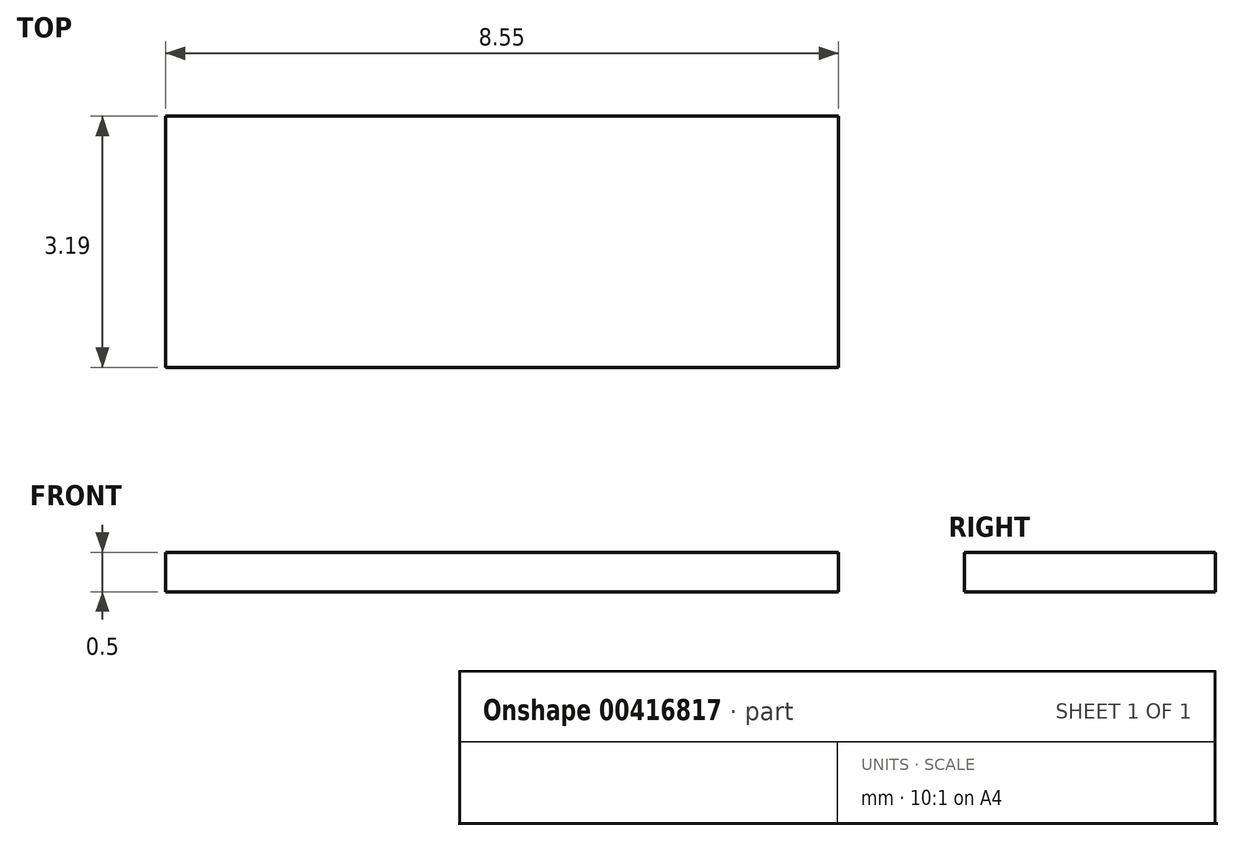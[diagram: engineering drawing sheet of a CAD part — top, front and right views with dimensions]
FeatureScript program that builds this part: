
annotation { "Feature Type Name" : "Feature", "Feature Type Description" : "" }
export const myFeature = defineFeature(function(context is Context, id is Id, definition is map)
    precondition{}
    {
        {
            var Q0;
            Q0=qCreatedBy(makeId("Top.planeOp"),FACE);
            var sketch = newSketch(context, id + "F0", { "sketchPlane" : qUnion([Q0])});
            skLineSegment(sketch, "E0.bottom", {"start": v(0, 0) * mm, "end": v(8.55, 0) * mm});
            skLineSegment(sketch, "E0.top", {"start": v(0, 3.19) * mm, "end": v(8.55, 3.19) * mm});
            skLineSegment(sketch, "E0.left", {"start": v(0, 0) * mm, "end": v(0, 3.19) * mm});
            skLineSegment(sketch, "E0.right", {"start": v(8.55, 0) * mm, "end": v(8.55, 3.19) * mm});
            skSolve(sketch);
        }
        {
            var Q0;
            Q0 = qSketchRegion(id + "F0", true);
            extrude(context, id + "F1", {"entities" : qUnion([Q0]), "depth" : .5 * mm, "offsetDistance" : 25.4 * mm});
        }
    });
